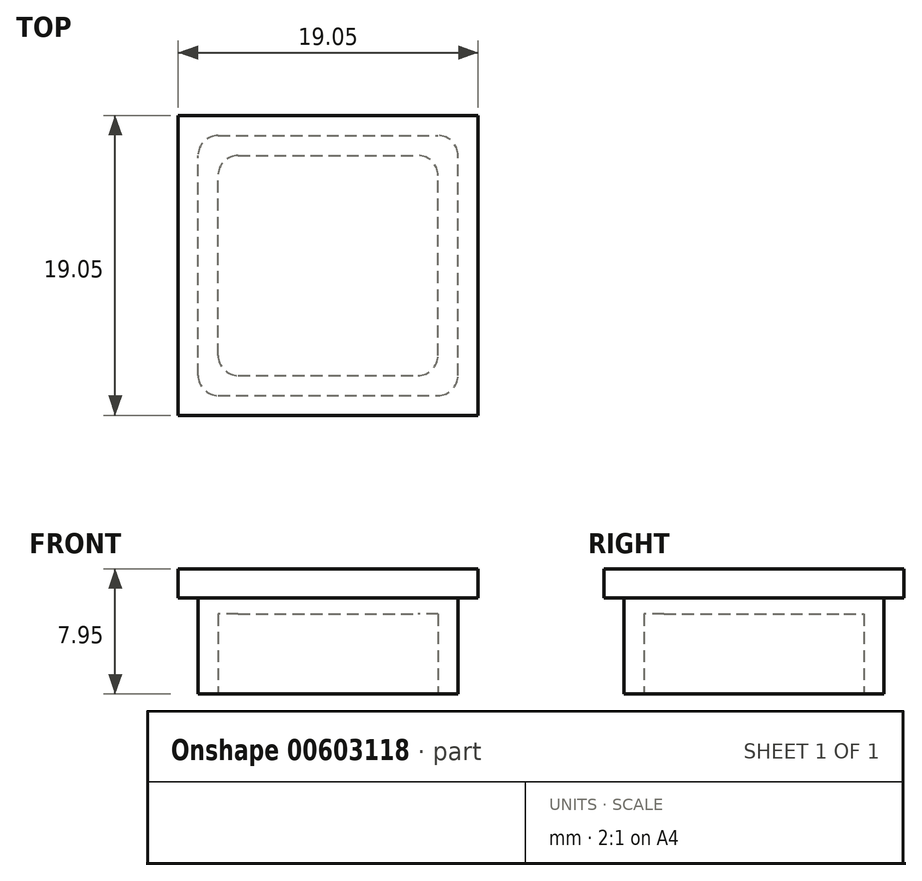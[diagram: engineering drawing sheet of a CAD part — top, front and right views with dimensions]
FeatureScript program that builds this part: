
annotation { "Feature Type Name" : "Feature", "Feature Type Description" : "" }
export const myFeature = defineFeature(function(context is Context, id is Id, definition is map)
    precondition{}
    {
        {
            var Q0;
            Q0=qCreatedBy(makeId("Top.planeOp"),FACE);
            var sketch = newSketch(context, id + "F0", { "sketchPlane" : qUnion([Q0])});
            skLineSegment(sketch, "E0.bottom", {"start": v(1.27, 0) * mm, "end": v(15.24, 0) * mm});
            skLineSegment(sketch, "E0.top", {"start": v(1.27, 16.51) * mm, "end": v(15.24, 16.51) * mm});
            skLineSegment(sketch, "E0.left", {"start": v(0, 1.27) * mm, "end": v(0, 15.24) * mm});
            skLineSegment(sketch, "E0.right", {"start": v(16.51, 1.27) * mm, "end": v(16.51, 15.24) * mm});
            skPoint(sketch, "E1.visualSharp", {"position": v(0, 16.51) * mm});
            skArc(sketch, "E1.filletArc", {"start": v(1.27, 16.51) * mm, "mid": v(0.37, 16.14) * mm, "end": v(0, 15.24) * mm});
            skPoint(sketch, "E2.visualSharp", {"position": v(16.51, 16.51) * mm});
            skArc(sketch, "E2.filletArc", {"start": v(16.51, 15.24) * mm, "mid": v(16.14, 16.14) * mm, "end": v(15.24, 16.51) * mm});
            skPoint(sketch, "E3.visualSharp", {"position": v(16.51, 0) * mm});
            skArc(sketch, "E3.filletArc", {"start": v(15.24, 0) * mm, "mid": v(16.14, 0.37) * mm, "end": v(16.51, 1.27) * mm});
            skPoint(sketch, "E4.visualSharp", {"position": v(0, 0) * mm});
            skArc(sketch, "E4.filletArc", {"start": v(0, 1.27) * mm, "mid": v(0.37, 0.37) * mm, "end": v(1.27, 0) * mm});
            skPoint(sketch, "E5", {"position": v(8.26, 8.26) * mm});
            skPoint(sketch, "E5.positionSnap0", {"position": v(16.51, 8.26) * mm});
            skPoint(sketch, "E5.positionSnap1", {"position": v(8.26, 0) * mm});
            skSolve(sketch);
        }
        {
            var Q0;
            Q0=qSketchRegion(id+"F0",true);
            extrude(context, id + "F1", {"entities" : qUnion([Q0]), "oppositeDirection" : true, "depth" : 6.1 * mm});
        }
        {
            var Q0;
            Q0=makeQuery(id+"F1.opExtrude","CAP_FACE",FACE,{"disambiguationData":[OSD([sQuery(id+"F0.wireOp",EDGE,"E0.bottom"),sQuery(id+"F0.wireOp",EDGE,"E0.top"),sQuery(id+"F0.wireOp",EDGE,"E0.left"),sQuery(id+"F0.wireOp",EDGE,"E0.right"),sQuery(id+"F0.wireOp",EDGE,"E1.filletArc"),sQuery(id+"F0.wireOp",EDGE,"E2.filletArc"),sQuery(id+"F0.wireOp",EDGE,"E3.filletArc"),sQuery(id+"F0.wireOp",EDGE,"E4.filletArc")])],"isStart":false});
            var sketch = newSketch(context, id + "F2", { "sketchPlane" : qUnion([Q0])});
            skLineSegment(sketch, "E6.bottom", {"start": v(2.54, -1.27) * mm, "end": v(13.97, -1.27) * mm});
            skLineSegment(sketch, "E6.top", {"start": v(2.54, -15.24) * mm, "end": v(13.97, -15.24) * mm});
            skLineSegment(sketch, "E6.left", {"start": v(1.27, -2.54) * mm, "end": v(1.27, -13.97) * mm});
            skLineSegment(sketch, "E6.right", {"start": v(15.24, -2.54) * mm, "end": v(15.24, -13.97) * mm});
            skPoint(sketch, "E7.visualSharp", {"position": v(1.27, -1.27) * mm});
            skArc(sketch, "E7.filletArc", {"start": v(2.54, -1.27) * mm, "mid": v(1.64, -1.64) * mm, "end": v(1.27, -2.54) * mm});
            skPoint(sketch, "E8.visualSharp", {"position": v(15.24, -1.27) * mm});
            skArc(sketch, "E8.filletArc", {"start": v(15.24, -2.54) * mm, "mid": v(14.87, -1.64) * mm, "end": v(13.97, -1.27) * mm});
            skPoint(sketch, "E9.visualSharp", {"position": v(15.24, -15.24) * mm});
            skArc(sketch, "E9.filletArc", {"start": v(13.97, -15.24) * mm, "mid": v(14.87, -14.87) * mm, "end": v(15.24, -13.97) * mm});
            skPoint(sketch, "E10.visualSharp", {"position": v(1.27, -15.24) * mm});
            skArc(sketch, "E10.filletArc", {"start": v(1.27, -13.97) * mm, "mid": v(1.64, -14.87) * mm, "end": v(2.54, -15.24) * mm});
            skSolve(sketch);
        }
        {
            var Q0;
            Q0=qSketchRegion(id+"F2",true);
            extrude(context, id + "F3", {"entities" : qUnion([Q0]), "operationType" : NewBodyOperationType.REMOVE, "oppositeDirection" : true, "depth" : 5.08 * mm});
        }
        {
            var Q0;
            Q0=qCreatedBy(makeId("Top.planeOp"),FACE);
            var sketch = newSketch(context, id + "F4", { "sketchPlane" : qUnion([Q0])});
            skLineSegment(sketch, "E11.bottom", {"start": v(-1.27, 17.78) * mm, "end": v(17.78, 17.78) * mm});
            skLineSegment(sketch, "E11.top", {"start": v(-1.27, -1.27) * mm, "end": v(17.78, -1.27) * mm});
            skLineSegment(sketch, "E11.left", {"start": v(-1.27, 17.78) * mm, "end": v(-1.27, -1.27) * mm});
            skLineSegment(sketch, "E11.right", {"start": v(17.78, 17.78) * mm, "end": v(17.78, -1.27) * mm});
            skSolve(sketch);
        }
        {
            var Q0;
            Q0=qSketchRegion(id+"F4",true);
            extrude(context, id + "F5", {"entities" : qUnion([Q0]), "operationType" : NewBodyOperationType.ADD, "depth" : 1.85 * mm});
        }
    });
